# Revit family: Electronics_Controls_Biamp_Tesira_Hardware-Dialer_HD-1__
name_source: partatom
category: Communication Devices
units: mm (PartAtom-declared; Revit-internal decimal feet)

## family parameters
Cut with Voids When Loaded = No
Host = Face
Maintain Annotation Orientation = No
OmniClass Number = 23.85.10.11.14
OmniClass Title = Audio Equipment
Part Type = Normal
Room Calculation Point = No
Round Connector Dimension = Use Diameter
Shared = No

## types (1)
- HD-1
    Altitude = 0-10,000 ft (0-3000m) MSL
    Apparent Load = 0 VA
    Buttons = 12-key standard dial pad, 4 context (soft) buttons, 13 dedicated buttons
    Compatibility = Tesira SERVER and SERVER-IO, with STC-2 or SVC-2 cards installed, TesiraFORTÉ VT (all models), TesiraFORTÉ VT4 (all models), TesiraFORTÉ X (all models)
    Compliance = FCC Part 15B (USA), CE Marked* (Europe), UL and C-UL (USA and Canada), RCM (Australia), EAC (Eurasian Customs Union), RoHS Directive (Europe), KCC (Korea)
    Connector Description = PoE (IEEE 802.3at Class 1, 4W)
    Control Programming = Tesira Design Software
    Data/Control Cable Length = Up to 330ft (100m)
    Default Elevation = 4' - 0"
    Depth = 0' - 5 11/16"
    Description = Tesira® HD-1 Hardware Dialer
    Display Diagonal Size = 2.7 inch
    Height = 0' - 1 9/16"
    Housing Material = Biamp - Plastic - Dark Gray
    Humidity = 0-95% relative humidity (non-condensing)
    Manufacturer = Biamp
    Max Power Consumption = 0 W
    Model = Tesira HD-1
    Network Connection = RJ-45 with Ethernet cable (CAT5, CAT5e, CAT6, or CAT7)
    Number of Poles = 1
    Power Factor = 1
    Product Documentation Link = https://downloads.biamp.com
    Product Page URL = https://www.biamp.com
    Product data url = https://www.bimobject.com
    Temperature Range = 32 - 104° F (0 - 40° C)
    URL = https://www.biamp.com
    Voltage = 0 V
    Weight = 0.90 lbf
    Width = 0' - 5 11/16"

## geometry (parser evidence)
native form markers: Sweep x2
no freeform markers — native parametric forms only
